# Revit family: LZ.OPL ECO LED
name_source: partatom
category: Осветительные приборы
revit_build: Autodesk Revit 2016 (Build: 20150220_1215(x64)
units: mm (PartAtom-declared; Revit-internal decimal feet)

## family parameters
Источник света = Да
Общий = Нет
Основа = Грань
При загрузке вырезать с полостями = Нет
Размер круглого соединителя = Использовать диаметр
Тип детали = Нормальный
Точка расчета площади = Нет

## types (1)
- LZ.OPL ECO LED
    ADSK_Единица измерения = Шт.
    ADSK_Завод-изготовитель = ООО МГК Световые технологии
    ADSK_Код изделия = 1074000600
    ADSK_Количество фаз = 1
    ADSK_Количество фаз числовое = 1
    ADSK_Коэффициент мощности = 0.9
    ADSK_Масса = 3.7
    ADSK_Наименование = Серия светильников со степенью защиты IP65 и высокой светоотдачей для освещения небольших производственных цехов, автомастерских и паркингов. Быстрый и удобный монтаж на опорную поверхность благодаря монтажным пластинам. Большое количество модификаций, различающихся габаритными размерами и световым потоком, для замены светильников типа ЛСП
    ADSK_Напряжение = 230 В
    ADSK_Номинальная мощность = 0 кВт
    ADSK_Полная мощность = 0 кВ·А
    ADSK_Размер_Высота = 103 мм
    ADSK_Размер_Длина = 1270 мм
    ADSK_Размер_Ширина = 173 мм
    ADSK_Ток = 0 А
    ADSK_Энергоэффективность = 76 лм/Вт
    IP Class = IP65
    URL = https://www.ltcompany.com
    Блок аварийного питания = Нет
    Видимая форма излучения при визуализации = Нет
    Группа модели = Светильники
    Изготовитель = ООО МГК Световые технологии
    Излучение по длине прямоугольника = 1270 мм
    Излучение по ширине прямоугольника = 173 мм
    Класс Защиты = II
    Класс пожароопасности = П-I,II,IIa,ІІІ
    Климатическая зона = УХЛ2
    Код по классификатору = D5020200
    Корпус = Серый пластик
    Крепление = 5 мм
    Область использования = Промышленные предприятия, Складские объекты
    Описание = Серия светильников со степенью защиты IP65 и высокой светоотдачей для освещения небольших производственных цехов, автомастерских и паркингов. Быстрый и удобный монтаж на опорную поверхность благодаря монтажным пластинам. Большое количество модификаций, различающихся габаритными размерами и световым потоком, для замены светильников типа ЛСП
    Отметка по умолчанию = 0 мм
    Плафон = Плафон самосвечение
    Подвес ширина = 800 мм
    Подвес.материал = Корпус металл
    Полная установленная мощность = 0 кВ·А
    Разработчик = ООО ПРОРУБИМ
    Разработчик (телефон) = +7 (495) 649-85-43
    Светофильтр = 16777215
    Смещение цветовой температуры при затухании лампы = <Нет>
    Тип ИС = LED
    Тип ПРА = Драйвер
    Тип продукции = Светильник
    Угол наклона = -90.00°
    Файл фотометрической сетки = generic

## geometry (parser evidence)
native form markers: Blend x2
no freeform markers — native parametric forms only
